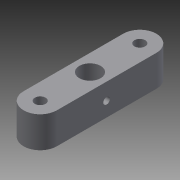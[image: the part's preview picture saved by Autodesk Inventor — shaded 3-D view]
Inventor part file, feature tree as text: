
AUTODESK INVENTOR PART (.ipt)
format: ipt  version: 2015 (Build 190159000, 159)  size: 104,960 bytes
history: native  units: in
note: dims shown in document units (in); Inventor stores cm internally (conversion verified against a paired STEP export)
features: extrude x2, sketch x2
ambient origin geometry x8: Origin, YZ Plane, XZ Plane, XY Plane, X Axis, Y Axis, Z Axis, Center Point
bodies: Body1 (feature_tree)
feature tree (4):
  extrude  "Extrusion3"  Depth=0.4055in
  extrude  "Extrusion4"  Depth=0.9449in
  sketch  "Sketch1"  dims[d0=0.248in d5=0.4055in]
  sketch  "Sketch3"  dims[d15=0.9449in d16=0.9449in d17=0.2047in d18=0.2047in d19=0.6299in d20=0.6299in d21=0.6299in d22=0.315in d23=0.315in d24=0.5906in d25=0.0in d26=0.2756in d27=0.126in d28=1.1811in d29=0.0in]
